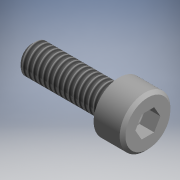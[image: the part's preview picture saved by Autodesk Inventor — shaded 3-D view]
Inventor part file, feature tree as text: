
AUTODESK INVENTOR PART (.ipt)
format: ipt  version: 2017.3 (Build 213256000, 256)  size: 130,560 bytes
history: native  units: mm (DEFAULTED — no unit token found)
features: other x7, sketch x3, revolve x2, thread x1, extrude x1
ambient origin geometry x8: Origin, YZ Plane, XZ Plane, XY Plane, X Axis, Y Axis, Z Axis, Center Point
bodies: Solid1 (feature_tree)
feature tree (14):
  revolve  "Revolution1"  [1 undecoded]
  thread  "Thread1"  [1 undecoded]
  extrude  "Extrusion1"  TaperAngle=0.0deg  [1 undecoded]
  revolve  "Revolution2"  [1 undecoded]
  other  "SCW_XY"
  other  "SCW_YZ"
  other  "SCW_ZX"
  other  "SCW_X"
  other  "SCW_Y"
  other  "SCW_Z"
  other  "SCW_Center"
  sketch  "Sketch_1"  dims[d0=360.0deg d1=10.714mm d2=0.0mm d3=2.0mm d4=0.0mm]
  sketch  "Sketch_2"  dims[d5=360.0deg d6=0.0mm]
  sketch  "Sketch_5"
note: 4 required parameter values undecoded (feature->parameter linkage not recoverable at this tier; creation-order binding heuristic only, values carry confidence <= 0.55)